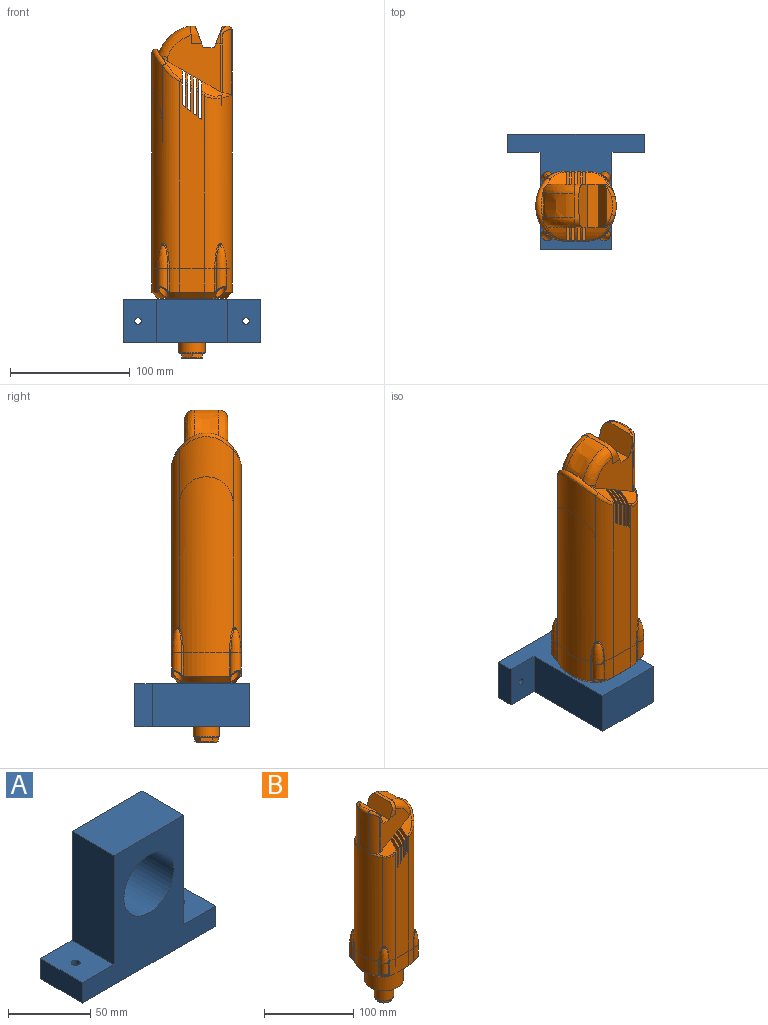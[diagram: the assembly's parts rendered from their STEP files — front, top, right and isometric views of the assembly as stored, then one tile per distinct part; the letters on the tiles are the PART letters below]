
ASSEMBLY  parts=2 mates=1
PART A: 13 faces, bbox 114x36x96 mm
  f0: plane 114x36mm, normal (0,0,-1), area 4056.5mm2, adj f1,f8,f9,f10,f11,f12
  f1: plane 36x15mm, normal (1,0,0), area 540mm2, adj f0,f2,f9,f10
  f2: plane 36x27mm, normal (0,0,1), area 948.2mm2, adj f1,f3,f9,f10,f12
  f3: plane 81x36mm, normal (1,0,0), area 2916mm2, adj f2,f4,f9,f10
  f4: plane 60x36mm, normal (0,0,1), area 2160mm2, adj f3,f5,f9,f10
  f5: plane 81x36mm, normal (-1,0,0), area 2916mm2, adj f4,f6,f9,f10
  f6: plane 36x27mm, normal (0,0,1), area 948.2mm2, adj f5,f8,f9,f10,f11
  f7: cylinder r=21.5mm len=43mm, axis (0,1,0), area 4863.2mm2, adj f9,f10
  f8: plane 36x15mm, normal (-1,0,0), area 540mm2, adj f0,f6,f9,f10
  f9: plane 114x96mm, normal (0,-1,0), area 5117.8mm2, adj f0,f1,f2,f3,f4,f5,f6,f7
  f10: plane 114x96mm, normal (0,1,0), area 5117.8mm2, adj f0,f1,f2,f3,f4,f5,f6,f7
  f11: cylinder r=2.75mm len=15mm, axis (0,0,-1), area 259.2mm2, adj f0,f6
  f12: cylinder r=2.75mm len=15mm, axis (0,0,-1), area 259.2mm2, adj f0,f2
PART B: 167 faces, bbox 76.6x68.5x277.2 mm
  f0: cylinder r=33.5mm len=44.67mm, axis (0,0,-1), area 1328.8mm2, adj f32,f35,f43,f72
  f1: cylinder r=40mm len=10.11mm, axis (0.87,0,0.5), area 28.1mm2, adj f3,f57,f160,f164
  f2: cylinder r=40mm len=10.11mm, axis (0.87,0,0.5), area 28.1mm2, adj f4,f60,f160,f164
  f3: cylinder r=3mm len=4.08mm, axis (0.87,0,0.5), area 5.3mm2, adj f1,f53,f160,f164
  f4: cylinder r=3mm len=4.08mm, axis (0.87,0,0.5), area 5.3mm2, adj f2,f54,f160,f164
  f5: cylinder r=40mm len=10.11mm, axis (0.87,0,0.5), area 28.1mm2, adj f7,f57,f153,f165
  f6: cylinder r=40mm len=10.11mm, axis (0.87,0,0.5), area 28.1mm2, adj f8,f60,f153,f165
  f7: cylinder r=3mm len=4.08mm, axis (0.87,0,0.5), area 5.3mm2, adj f5,f53,f153,f165
  f8: cylinder r=3mm len=4.08mm, axis (0.87,0,0.5), area 5.3mm2, adj f6,f54,f153,f165
  f9: cylinder r=40mm len=10.11mm, axis (0.87,0,0.5), area 28.1mm2, adj f11,f57,f152,f155
  f10: cylinder r=40mm len=10.11mm, axis (0.87,0,0.5), area 28.1mm2, adj f12,f60,f152,f155
  f11: cylinder r=3mm len=4.08mm, axis (0.87,0,0.5), area 5.3mm2, adj f9,f53,f152,f155
  f12: cylinder r=3mm len=4.08mm, axis (0.87,0,0.5), area 5.3mm2, adj f10,f54,f152,f155
  f13: cylinder r=40mm len=24.77mm, axis (0.87,0,0.5), area 168.7mm2, adj f15,f57,f58,f71,f72,f156
  f14: cylinder r=40mm len=24.77mm, axis (0.87,0,0.5), area 168.7mm2, adj f16,f59,f60,f72,f73,f156
  f15: cylinder r=3mm len=3.01mm, axis (0.87,0,0.5), area 3.9mm2, adj f13,f53,f71,f156
  f16: cylinder r=3mm len=3.01mm, axis (0.87,0,0.5), area 3.9mm2, adj f14,f54,f73,f156
  f17: plane 20.12x20mm, normal (0,1,0), area 402.5mm2, adj f18,f22,f54,f55
  f18: cylinder r=20mm len=20mm, axis (0,0,-1), area 183.4mm2, adj f17,f39,f40,f119
  f19: cone r=5mm half-angle=0deg, axis (0,0,-1), area 0mm2, adj f107,f108,f124
  f20: cone r=5mm half-angle=0deg, axis (0,0,-1), area 0mm2, adj f107,f108,f121
  f21: cylinder r=33.5mm len=146.32mm, axis (0,0,-1), area 6933.1mm2, adj f37,f39,f41,f65,f68,f76,f123,f124
  f22: cylinder r=20mm len=20mm, axis (0,0,-1), area 183.4mm2, adj f17,f35,f36,f143
  f23: cone r=5mm half-angle=0deg, axis (0,0,-1), area 0mm2, adj f109,f110,f145
  f24: cone r=5mm half-angle=0deg, axis (0,0,-1), area 0mm2, adj f109,f110,f148
  f25: cone r=5mm half-angle=0deg, axis (0,0,-1), area 0mm2, adj f105,f106,f129
  f26: cone r=5mm half-angle=0deg, axis (0,0,-1), area 0mm2, adj f105,f106,f132
  f27: cylinder r=20mm len=20mm, axis (0,0,-1), area 183.4mm2, adj f28,f41,f42,f127
  f28: plane 20.12x20mm, normal (0,-1,0), area 402.5mm2, adj f27,f29,f53,f56
  f29: cylinder r=20mm len=20mm, axis (0,0,-1), area 183.4mm2, adj f28,f43,f44,f135
  f30: cone r=5mm half-angle=0deg, axis (0,0,-1), area 0mm2, adj f103,f104,f140
  f31: cone r=5mm half-angle=0deg, axis (0,0,-1), area 0mm2, adj f103,f104,f137
  f32: cylinder r=33.5mm len=146.33mm, axis (0,0,-1), area 6782.4mm2, adj f0,f33,f35,f43,f139,f140,f141,f147
  f33: cylinder r=33.5mm len=38.46mm, axis (0,0,-1), area 819.2mm2, adj f32,f34,f142,f150
  f34: cone r=33.5mm half-angle=45deg, axis (0,0,1), area 314.3mm2, adj f33,f36,f44,f51,f104,f110,f112,f118
  f35: cylinder r=20mm len=168.29mm, axis (0,0,-1), area 2582.9mm2, adj f0,f22,f32,f54,f73,f144,f145,f146
  f36: cone r=15mm half-angle=45deg, axis (0,0,1), area 92.2mm2, adj f22,f34,f51,f55,f110,f112,f143
  f37: cylinder r=33.5mm len=38.46mm, axis (0,0,-1), area 819.2mm2, adj f21,f38,f126,f134
  f38: cone r=33.5mm half-angle=45deg, axis (0,0,1), area 314.2mm2, adj f37,f40,f42,f51,f106,f108,f114,f116
  f39: cylinder r=20mm len=144.06mm, axis (0,0,-1), area 2256.6mm2, adj f18,f21,f54,f75,f120,f121,f122
  f40: cone r=15mm half-angle=45deg, axis (0,0,1), area 92.2mm2, adj f18,f38,f51,f55,f108,f114,f119
  f41: cylinder r=20mm len=144.06mm, axis (0,0,-1), area 2256.6mm2, adj f21,f27,f53,f69,f128,f129,f130
  f42: cone r=15mm half-angle=45deg, axis (0,0,1), area 92.2mm2, adj f27,f38,f51,f56,f106,f116,f127
  f43: cylinder r=20mm len=168.29mm, axis (0,0,-1), area 2582.9mm2, adj f0,f29,f32,f53,f71,f136,f137,f138
  f44: cone r=15mm half-angle=45deg, axis (0,0,1), area 92.2mm2, adj f29,f34,f51,f56,f104,f118,f135
  f45: plane 20.7x20.7mm, normal (0,0,-1), area 86.3mm2, adj f91,f92,f93,f94,f95,f96,f97
  f46: plane 43x43mm, normal (0,0,-1), area 1245.8mm2, adj f52,f85,f86,f87,f88
  f47: bspline ~36x15mm, area 152.6mm2, adj f57,f60,f78,f79,f80,f84
  f48: cylinder r=40mm len=24.03mm, axis (0.87,0,0.5), area 201.2mm2, adj f57,f66,f68,f69,f70,f77,f161
  f49: cylinder r=40mm len=20.71mm, axis (0.87,0,0.5), area 31.9mm2, adj f61,f62,f63,f72
  f50: cylinder r=40mm len=24.03mm, axis (0.87,0,0.5), area 201.2mm2, adj f60,f67,f74,f75,f76,f81,f161
  f51: plane 57x48mm, normal (0,0,-1), area 896.6mm2, adj f34,f36,f38,f40,f42,f44,f52,f55
  f52: cylinder r=21.5mm len=43mm, axis (0,0,-1), area 3242.1mm2, adj f46,f51
  f53: plane 155.68x20.12mm, normal (0,-1,0), area 2809.7mm2, adj f3,f7,f11,f15,f28,f41,f43,f70
  f54: plane 155.68x20.12mm, normal (0,1,0), area 2809.7mm2, adj f4,f8,f12,f16,f17,f35,f39,f74
  f55: plane 20.12x5mm, normal (0,0.71,-0.71), area 142.3mm2, adj f17,f36,f40,f51
  f56: plane 20.12x5mm, normal (0,-0.71,-0.71), area 142.3mm2, adj f28,f42,f44,f51
  f57: plane 46.92x44.12mm, normal (0,-1,0), area 1195mm2, adj f1,f5,f9,f13,f47,f48,f58,f61
  f58: cylinder r=8mm len=5.27mm, axis (0,0,-1), area 9.7mm2, adj f13,f57,f61,f72
  f59: cylinder r=8mm len=5.27mm, axis (0,0,-1), area 9.7mm2, adj f14,f60,f63,f72
  f60: plane 46.92x44.12mm, normal (0,1,0), area 1195mm2, adj f2,f6,f10,f14,f47,f50,f59,f63
  f61: bspline ~27.78x26.09mm, area 425.8mm2, adj f49,f57,f58,f62,f64,f72
  f62: bspline ~27x25mm, area 708.7mm2, adj f49,f61,f63,f64
  f63: bspline ~27.78x26.09mm, area 425.8mm2, adj f49,f59,f60,f62,f64,f72
  f64: bspline ~36x15mm, area 304.7mm2, adj f57,f60,f61,f62,f63,f83
  f65: extruded ~54.69x16mm, area 855.6mm2, adj f21,f66,f67,f68,f76,f79
  f66: cylinder r=15mm len=54.58mm, axis (0,0,-1), area 662mm2, adj f48,f65,f68,f77,f78
  f67: cylinder r=15mm len=54.58mm, axis (0,0,-1), area 662mm2, adj f50,f65,f76,f80,f81
  f68: bspline ~21.02x11.51mm, area 35.1mm2, adj f21,f48,f65,f66,f69
  f69: bspline ~17.82x8.68mm, area 36.3mm2, adj f41,f48,f68,f70
  f70: cylinder r=3mm len=4.08mm, axis (0.87,0,0.5), area 6.8mm2, adj f48,f53,f69,f161
  f71: bspline ~20.18x18.27mm, area 69mm2, adj f13,f15,f43,f72
  f72: bspline ~49.8x19.15mm, area 312.8mm2, adj f0,f13,f14,f49,f58,f59,f61,f63
  f73: bspline ~18.18x17.34mm, area 69mm2, adj f14,f16,f35,f72
  f74: cylinder r=3mm len=4.08mm, axis (0.87,0,0.5), area 6.8mm2, adj f50,f54,f75,f161
  f75: bspline ~17.82x8.68mm, area 36.3mm2, adj f39,f50,f74,f76
  f76: bspline ~21.02x11.51mm, area 35.1mm2, adj f21,f50,f65,f67,f75
  f77: cylinder r=3mm len=40.53mm, axis (0,0,-1), area 59.3mm2, adj f48,f57,f66,f78
  f78: bspline ~31x12.04mm, area 64.8mm2, adj f47,f66,f77,f79
  f79: bspline ~16x3.89mm, area 73.7mm2, adj f47,f65,f78,f80
  f80: bspline ~31x12.04mm, area 64.9mm2, adj f47,f67,f79,f81
  f81: cylinder r=3mm len=40.53mm, axis (0,0,-1), area 59.3mm2, adj f50,f60,f67,f80
  f82: plane 36x9mm, normal (0,0,1), area 324mm2, adj f57,f60,f83,f84
  f83: plane 36x18mm, normal (-0.93,0,0.36), area 666.1mm2, adj f57,f60,f64,f82
  f84: plane 36x18mm, normal (0.93,0,0.36), area 665.8mm2, adj f47,f57,f60,f82
  f85: cylinder r=8.5mm len=13.9mm, axis (0,0,1), area 92.8mm2, adj f46,f86,f88,f89
  f86: plane 9.79x5.7mm, normal (-1,0,0), area 55.8mm2, adj f46,f85,f87,f89
  f87: cylinder r=8.5mm len=13.9mm, axis (0,0,1), area 92.8mm2, adj f46,f86,f88,f89
  f88: plane 9.79x5.7mm, normal (1,0,0), area 55.8mm2, adj f46,f85,f87,f89
  f89: plane 21.7x21.7mm, normal (0,0,1), area 163.5mm2, adj f85,f86,f87,f88,f90
  f90: cylinder r=10.85mm len=21.7mm, axis (0,0,1), area 1056.7mm2, adj f89,f91
  f91: cone r=10.35mm half-angle=45deg, axis (0,0,1), area 47.1mm2, adj f45,f90
  f92: plane 9.82x3.95mm, normal (-1,0,0), area 36.2mm2, adj f45,f93,f97,f98
  f93: plane 8.5x4.91mm, normal (-0.5,0.87,0), area 36.2mm2, adj f45,f92,f94,f98
  f94: plane 8.5x4.91mm, normal (0.5,0.87,0), area 36.2mm2, adj f45,f93,f95,f98
  f95: plane 9.82x3.95mm, normal (1,0,0), area 36.2mm2, adj f45,f94,f96,f98
  f96: plane 8.5x4.91mm, normal (0.5,-0.87,0), area 36.2mm2, adj f45,f95,f97,f98
  f97: plane 8.5x4.91mm, normal (-0.5,-0.87,0), area 36.2mm2, adj f45,f92,f96,f98
  f98: cone r=8.41mm half-angle=60deg, axis (0,0,1), area 32.1mm2, adj f92,f93,f94,f95,f96,f97,f99
  f99: plane 16.83x16.83mm, normal (0,0,-1), area 143.9mm2, adj f98,f102
  f100: plane 8x8mm, normal (0,0,-1), area 50.3mm2, adj f101
  f101: cylinder r=4mm len=24.7mm, axis (0,0,-1), area 620.8mm2, adj f100,f102
  f102: cone r=4mm half-angle=45deg, axis (0,0,-1), area 40mm2, adj f99,f101
  f103: revolved ~19.87x8.58mm, area 228.6mm2, adj f30,f31,f138,f139
  f104: cone r=5mm half-angle=0deg, axis (0,0,-1), area 253.1mm2, adj f30,f31,f34,f44,f135,f136,f141,f142
  f105: revolved ~19.87x8.58mm, area 228.6mm2, adj f25,f26,f130,f131
  f106: cone r=5mm half-angle=0deg, axis (0,0,-1), area 253.1mm2, adj f25,f26,f38,f42,f127,f128,f133,f134
  f107: revolved ~19.87x8.58mm, area 228.6mm2, adj f19,f20,f122,f123
  f108: cone r=5mm half-angle=0deg, axis (0,0,-1), area 253.1mm2, adj f19,f20,f38,f40,f119,f120,f125,f126
  f109: revolved ~19.87x8.58mm, area 228.6mm2, adj f23,f24,f146,f147
  f110: cone r=5mm half-angle=0deg, axis (0,0,-1), area 253.1mm2, adj f23,f24,f34,f36,f143,f144,f149,f150
  f111: plane 8x8mm, normal (0,0,-1), area 50.3mm2, adj f112
  f112: cylinder r=4mm len=18.63mm, axis (0,0,-1), area 379.2mm2, adj f34,f36,f111
  f113: plane 8x8mm, normal (0,0,-1), area 50.3mm2, adj f114
  f114: cylinder r=4mm len=18.63mm, axis (0,0,-1), area 379.2mm2, adj f38,f40,f113
  f115: plane 8x8mm, normal (0,0,-1), area 50.3mm2, adj f116
  f116: cylinder r=4mm len=18.63mm, axis (0,0,-1), area 379.2mm2, adj f38,f42,f115
  f117: plane 8x8mm, normal (0,0,-1), area 50.3mm2, adj f118
  f118: cylinder r=4mm len=19mm, axis (0,0,-1), area 373.6mm2, adj f34,f44,f117
  f119: bspline ~41.83x1.17mm, area 24.8mm2, adj f18,f40,f108,f120
  f120: bspline ~15.97x1.17mm, area 0mm2, adj f39,f108,f119,f121
  f121: bspline ~15.97x1.17mm, area 0mm2, adj f20,f39,f120,f122
  f122: bspline ~21.74x6.08mm, area 29.2mm2, adj f39,f107,f121,f123
  f123: bspline ~22.87x4.26mm, area 26mm2, adj f21,f107,f122,f124
  f124: bspline ~15.97x1.22mm, area 0mm2, adj f19,f21,f123,f125
  f125: bspline ~15.97x1.22mm, area 0mm2, adj f21,f108,f124,f126
  f126: bspline ~51.97x1.23mm, area 25.7mm2, adj f37,f38,f108,f125
  f127: bspline ~29.94x1.17mm, area 24.8mm2, adj f27,f42,f106,f128
  f128: bspline ~15.97x1.17mm, area 0mm2, adj f41,f106,f127,f129
  f129: bspline ~15.97x1.17mm, area 0mm2, adj f25,f41,f128,f130
  f130: bspline ~23.35x6.44mm, area 29.2mm2, adj f41,f105,f129,f131
  f131: bspline ~20.82x4.01mm, area 26mm2, adj f21,f105,f130,f132
  f132: bspline ~15.97x1.22mm, area 0mm2, adj f21,f26,f131,f133
  f133: bspline ~15.97x1.22mm, area 0mm2, adj f21,f106,f132,f134
  f134: bspline ~31.97x1.23mm, area 25.7mm2, adj f37,f38,f106,f133
  f135: bspline ~41.78x1.17mm, area 24.8mm2, adj f29,f44,f104,f136
  f136: bspline ~15.97x1.17mm, area 0mm2, adj f43,f104,f135,f137
  f137: bspline ~15.97x1.17mm, area 0mm2, adj f31,f43,f136,f138
  f138: bspline ~21.74x6.08mm, area 29.2mm2, adj f43,f103,f137,f139
  f139: bspline ~22.87x4.26mm, area 26mm2, adj f32,f103,f138,f140
  f140: bspline ~15.97x1.22mm, area 0mm2, adj f30,f32,f139,f141
  f141: bspline ~15.97x1.22mm, area 0mm2, adj f32,f104,f140,f142
  f142: bspline ~51.97x1.23mm, area 25.7mm2, adj f33,f34,f104,f141
  f143: bspline ~29.94x1.17mm, area 24.8mm2, adj f22,f36,f110,f144
  f144: bspline ~15.97x1.17mm, area 0mm2, adj f35,f110,f143,f145
  f145: bspline ~15.97x1.17mm, area 0mm2, adj f23,f35,f144,f146
  f146: bspline ~23.35x6.44mm, area 29.2mm2, adj f35,f109,f145,f147
  f147: bspline ~20.82x4.01mm, area 26mm2, adj f32,f109,f146,f148
  f148: bspline ~15.97x1.22mm, area 0mm2, adj f24,f32,f147,f149
  f149: bspline ~15.97x1.22mm, area 0mm2, adj f32,f110,f148,f150
  f150: bspline ~31.97x1.23mm, area 25.7mm2, adj f33,f34,f110,f149
  f151: plane 36x2.6mm, normal (0.5,0,-0.87), area 108.1mm2, adj f57,f60,f152,f153
  f152: plane 58.46x30.47mm, normal (-1,0,0), area 1649.3mm2, adj f9,f10,f11,f12,f53,f54,f151,f154
  f153: plane 58.46x30.96mm, normal (1,0,0), area 1677.5mm2, adj f5,f6,f7,f8,f53,f54,f151,f154
  f154: plane 58x2.6mm, normal (-0.61,0,0.79), area 189.8mm2, adj f53,f54,f152,f153
  f155: plane 58.46x30.11mm, normal (1,0,0), area 1628.2mm2, adj f9,f10,f11,f12,f53,f54,f157,f158
  f156: plane 58.46x29.62mm, normal (-1,0,0), area 1600mm2, adj f13,f14,f15,f16,f53,f54,f157,f158
  f157: plane 36x2.6mm, normal (0.5,0,-0.87), area 108.1mm2, adj f57,f60,f155,f156
  f158: plane 58x2.6mm, normal (-0.61,0,0.79), area 189.8mm2, adj f53,f54,f155,f156
  f159: plane 36x2.6mm, normal (0.5,0,-0.87), area 108.1mm2, adj f57,f60,f160,f161
  f160: plane 58.46x32.17mm, normal (-1,0,0), area 1747.8mm2, adj f1,f2,f3,f4,f53,f54,f159,f162
  f161: plane 58.46x32.66mm, normal (1,0,0), area 1776mm2, adj f48,f50,f53,f54,f70,f74,f159,f162
  f162: plane 58x2.6mm, normal (-0.61,0,0.79), area 189.8mm2, adj f53,f54,f160,f161
  f163: plane 36x2.6mm, normal (0.5,0,-0.87), area 108.1mm2, adj f57,f60,f164,f165
  f164: plane 58.46x31.81mm, normal (1,0,0), area 1726.7mm2, adj f1,f2,f3,f4,f53,f54,f163,f166
  f165: plane 58.46x31.32mm, normal (-1,0,0), area 1698.6mm2, adj f5,f6,f7,f8,f53,f54,f163,f166
  f166: plane 58x2.6mm, normal (-0.61,0,0.79), area 189.8mm2, adj f53,f54,f164,f165
PLACE A rot(axis=(0,0.71,-0.71),180deg) t=(-145.2,82.17,333.3)mm
PLACE B rot(axis=(0,0,-1),180deg) t=(-145.2,22.17,346.3)mm
MATE fastened B.f0 <-> A.f7  axis (0,0,-1) through (-145.2,22.17,358.3)mm
